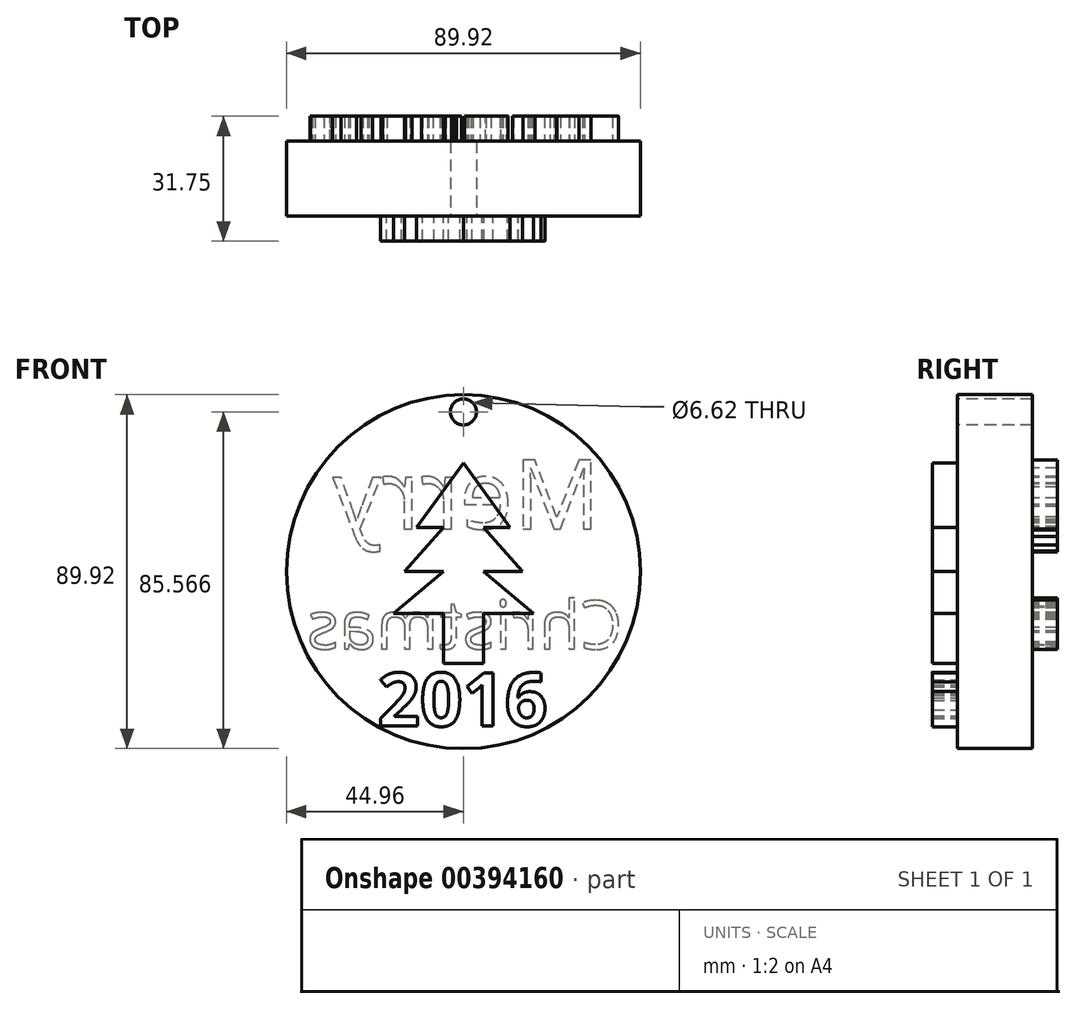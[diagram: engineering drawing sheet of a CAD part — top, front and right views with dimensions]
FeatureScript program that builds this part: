
annotation { "Feature Type Name" : "Feature", "Feature Type Description" : "" }
export const myFeature = defineFeature(function(context is Context, id is Id, definition is map)
    precondition{}
    {
        {
            var Q0;
            Q0=qCreatedBy(makeId("Front.planeOp"),FACE);
            var sketch = newSketch(context, id + "F0", { "sketchPlane" : qUnion([Q0])});
            skCircle(sketch, "E0", {"center": v(0, 0) * mm, "radius": 44.96 * mm});
            skSolve(sketch);
        }
        {
            var Q0;
            Q0=makeQuery(id+"F0.imprint","IMPRINT",FACE,{"disambiguationData":[TD([[makeQuery(id+"F0.imprint","IMPRINT",EDGE,{"derivedFrom":sQuery(id+"F0.wireOp",EDGE,"E0")}),1.0]])]});
            var sketch = newSketch(context, id + "F1", { "sketchPlane" : qUnion([Q0])});
            skLineSegment(sketch, "E1", {"start": v(0, -23.31) * mm, "end": v(-5.08, -23.31) * mm});
            skLineSegment(sketch, "E2", {"start": v(0, -23.31) * mm, "end": v(5.08, -23.31) * mm});
            skLineSegment(sketch, "E3", {"start": v(-5.08, -23.31) * mm, "end": v(-5.08, -10.61) * mm});
            skLineSegment(sketch, "E4", {"start": v(-5.08, -10.61) * mm, "end": v(-17.76, -10.61) * mm});
            skLineSegment(sketch, "E5", {"start": v(-17.76, -10.61) * mm, "end": v(-5.08, 0) * mm});
            skLineSegment(sketch, "E6", {"start": v(-5.08, 0) * mm, "end": v(-14.98, 0) * mm});
            skLineSegment(sketch, "E7", {"start": v(-14.98, 0) * mm, "end": v(-5.08, 11.2) * mm});
            skLineSegment(sketch, "E8", {"start": v(-5.08, 11.2) * mm, "end": v(-11.84, 11.2) * mm});
            skLineSegment(sketch, "E9", {"start": v(-11.84, 11.2) * mm, "end": v(0, 27.66) * mm});
            skLineSegment(sketch, "E10", {"start": v(5.08, -23.31) * mm, "end": v(5.08, -10.61) * mm});
            skLineSegment(sketch, "E11", {"start": v(5.08, -10.61) * mm, "end": v(17.76, -10.61) * mm});
            skLineSegment(sketch, "E12", {"start": v(17.76, -10.61) * mm, "end": v(5.08, 0) * mm});
            skLineSegment(sketch, "E13", {"start": v(5.08, 0) * mm, "end": v(14.98, 0) * mm});
            skLineSegment(sketch, "E14", {"start": v(14.98, 0) * mm, "end": v(5.08, 11.2) * mm});
            skLineSegment(sketch, "E15", {"start": v(5.08, 11.2) * mm, "end": v(11.84, 11.2) * mm});
            skLineSegment(sketch, "E16", {"start": v(11.84, 11.2) * mm, "end": v(0, 27.66) * mm});
            skSolve(sketch);
        }
        {
            var Q0;
            Q0 = qSketchRegion(id + "F1", true);
            extrude(context, id + "F2", {"entities" : qUnion([Q0]), "depth" : 25.4 * mm});
        }
        {
            var Q0;
            Q0 = qSketchRegion(id + "F0", true);
            extrude(context, id + "F3", {"entities" : qUnion([Q0]), "operationType" : NewBodyOperationType.ADD, "depth" : 19.05 * mm});
        }
        {
            var Q0;
            Q0=makeQuery(id+"F3.opExtrude","CAP_FACE",FACE,{"disambiguationData":[OSD([sQuery(id+"F0.wireOp",EDGE,"E0")])],"isStart":false});
            var sketch = newSketch(context, id + "F4", { "sketchPlane" : qUnion([Q0])});
            skCircle(sketch, "E17", {"center": v(0, 40.6) * mm, "radius": 3.3 * mm});
            skSolve(sketch);
        }
        {
            var Q0;
            Q0=makeQuery(id+"F4.imprint","IMPRINT",FACE,{"disambiguationData":[TD([[makeQuery(id+"F4.imprint","IMPRINT",EDGE,{"derivedFrom":sQuery(id+"F4.wireOp",EDGE,"E17")}),1.0]])]});
            extrude(context, id + "F5", {"entities" : qUnion([Q0]), "operationType" : NewBodyOperationType.REMOVE, "oppositeDirection" : true, "depth" : 80 * mm});
        }
        {
            var Q0;
            Q0=makeQuery(id+"F3.opExtrude","CAP_FACE",FACE,{"disambiguationData":[OSD([sQuery(id+"F0.wireOp",EDGE,"E0")])],"isStart":false});
            var sketch = newSketch(context, id + "F6", { "sketchPlane" : qUnion([Q0])});
            skText(sketch, "E18", { "text": "2016", "fontName": "OpenSans-Bold.ttf"});
            const initialGuessF6  = {"E18": [-0.0218, -0.03923, 1, 0, 0.0136]};
            skSetInitialGuess(sketch, initialGuessF6);
            skSolve(sketch);
        }
        {
            var Q0;
            Q0 = qSketchRegion(id + "F6", true);
            extrude(context, id + "F7", {"entities" : qUnion([Q0]), "operationType" : NewBodyOperationType.ADD, "depth" : 6.35 * mm});
        }
        {
            var Q0;
            Q0=makeQuery(id+"F3.boolean.opBoolean","MERGE",FACE,{"derivedFrom":[makeQuery(id+"F2.opExtrude","CAP_FACE",FACE,{"disambiguationData":[OSD([sQuery(id+"F1.wireOp",EDGE,"E1"),sQuery(id+"F1.wireOp",EDGE,"E2"),sQuery(id+"F1.wireOp",EDGE,"E3"),sQuery(id+"F1.wireOp",EDGE,"E4"),sQuery(id+"F1.wireOp",EDGE,"E5"),sQuery(id+"F1.wireOp",EDGE,"E6"),sQuery(id+"F1.wireOp",EDGE,"E7"),sQuery(id+"F1.wireOp",EDGE,"E8"),sQuery(id+"F1.wireOp",EDGE,"E9"),sQuery(id+"F1.wireOp",EDGE,"E10"),sQuery(id+"F1.wireOp",EDGE,"E11"),sQuery(id+"F1.wireOp",EDGE,"E12"),sQuery(id+"F1.wireOp",EDGE,"E13"),sQuery(id+"F1.wireOp",EDGE,"E14"),sQuery(id+"F1.wireOp",EDGE,"E15"),sQuery(id+"F1.wireOp",EDGE,"E16")])],"isStart":true}),makeQuery(id+"F3.opExtrude","CAP_FACE",FACE,{"disambiguationData":[OSD([sQuery(id+"F0.wireOp",EDGE,"E0")])],"isStart":true})]});
            var sketch = newSketch(context, id + "F8", { "sketchPlane" : qUnion([Q0])});
            skText(sketch, "E19", { "text": "Merry ", "fontName": "OpenSans-Regular.ttf"});
            skText(sketch, "E20", { "text": "Christmas", "fontName": "OpenSans-Regular.ttf"});
            const initialGuessF8  = {"E19": [-0.03479, 0.0109, 1, 0, 0.01759], "E20": [-0.04046, -0.0196, 1, 0, 0.01229]};
            skSetInitialGuess(sketch, initialGuessF8);
            skSolve(sketch);
        }
        {
            var Q0;
            Q0 = qSketchRegion(id + "F8", true);
            extrude(context, id + "F9", {"entities" : qUnion([Q0]), "operationType" : NewBodyOperationType.ADD, "depth" : 6.35 * mm});
        }
    });
